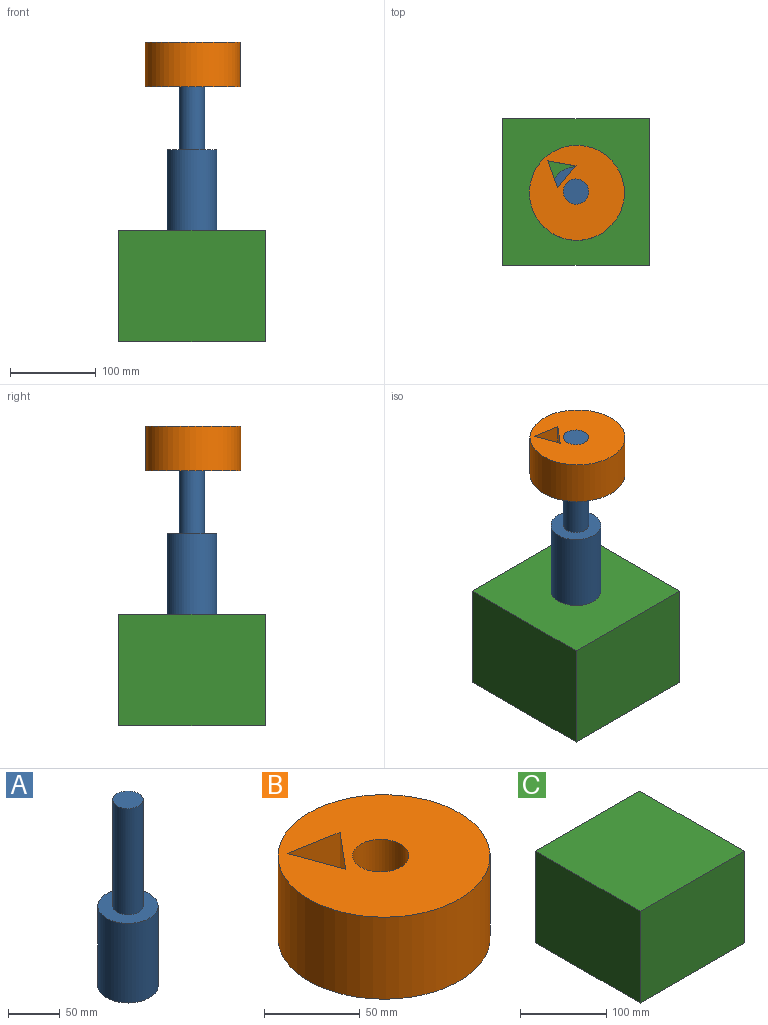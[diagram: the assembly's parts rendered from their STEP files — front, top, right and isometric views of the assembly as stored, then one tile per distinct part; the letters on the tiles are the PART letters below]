
ASSEMBLY  parts=3 mates=2
PART A: 5 faces, bbox 58.4x58.4x220.1 mm
  f0: cylinder r=29.2mm len=94.28mm, axis (0,0,-1), area 17296.8mm2, adj f1,f2
  f1: plane 58.4x58.4mm, normal (0,0,1), area 1998.4mm2, adj f0,f3
  f2: plane 58.4x58.4mm, normal (0,0,-1), area 2678.7mm2, adj f0
  f3: cylinder r=14.72mm len=125.81mm, axis (0,0,-1), area 11633.2mm2, adj f1,f4
  f4: plane 29.43x29.43mm, normal (0,0,1), area 680.4mm2, adj f3
PART B: 7 faces, bbox 111x111x52.6 mm
  f0: plane 111.03x111.03mm, normal (0,0,1), area 8511.9mm2, adj f2,f3,f4,f5,f6
  f1: plane 111.03x111.03mm, normal (0,0,-1), area 8511.9mm2, adj f2,f3,f4,f5,f6
  f2: cylinder r=55.52mm len=111.03mm, axis (0,0,-1), area 18330.8mm2, adj f0,f1
  f3: plane 52.55x33.13mm, normal (-0.17,-0.98,0), area 1768.1mm2, adj f0,f1,f4,f5
  f4: plane 52.55x31.62mm, normal (0.94,0.34,0), area 1768.1mm2, adj f0,f1,f3,f5
  f5: plane 52.55x25.77mm, normal (-0.77,0.64,0), area 1768.1mm2, adj f0,f1,f3,f4
  f6: cylinder r=14.72mm len=52.55mm, axis (0,0,1), area 4860.1mm2, adj f0,f1
PART C: 6 faces, bbox 170.9x171.4x130.4 mm
  f0: plane 171.36x130.38mm, normal (1,0,0), area 22342.3mm2, adj f1,f3,f4,f5
  f1: plane 170.94x130.38mm, normal (0,1,0), area 22288.2mm2, adj f0,f2,f4,f5
  f2: plane 171.36x130.38mm, normal (-1,0,0), area 22342.3mm2, adj f1,f3,f4,f5
  f3: plane 170.94x130.38mm, normal (0,-1,0), area 22288.2mm2, adj f0,f2,f4,f5
  f4: plane 171.36x170.94mm, normal (0,0,-1), area 29293mm2, adj f0,f1,f2,f3
  f5: plane 171.36x170.94mm, normal (0,0,1), area 29293mm2, adj f0,f1,f2,f3
PLACE A t=(83.85,-149.24,71.91)mm
PLACE B t=(83.85,-149.24,218.58)mm
PLACE C t=(83.85,-149.24,-40.42)mm
MATE revolute B.f6 <-> A.f0  axis (0,0,1) through (83.85,-149.24,244.86)mm
MATE fastened C.f5 <-> A.f0  axis (0,0,1) through (83.85,-149.24,24.77)mm
